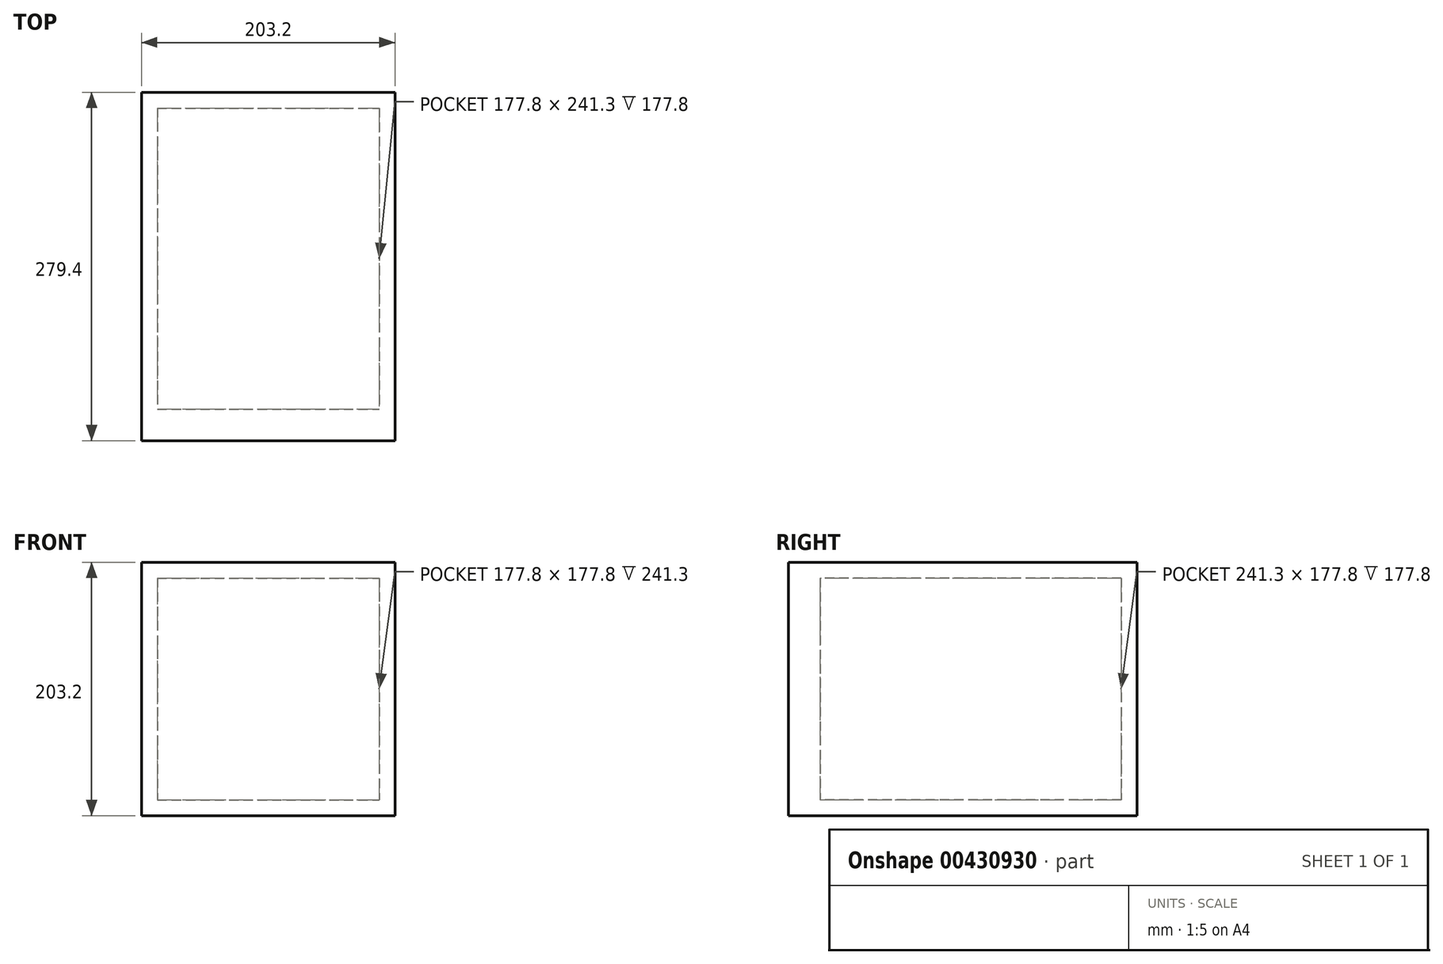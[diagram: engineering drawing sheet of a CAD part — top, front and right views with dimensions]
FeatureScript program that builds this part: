
annotation { "Feature Type Name" : "Feature", "Feature Type Description" : "" }
export const myFeature = defineFeature(function(context is Context, id is Id, definition is map)
    precondition{}
    {
        {
            var Q0;
            Q0=qCreatedBy(makeId("Top.planeOp"),FACE);
            var sketch = newSketch(context, id + "F0", { "sketchPlane" : qUnion([Q0])});
            skLineSegment(sketch, "E0.bottom", {"start": v(-126.86, 139.6) * mm, "end": v(76.34, 139.6) * mm});
            skLineSegment(sketch, "E0.top", {"start": v(-126.86, -114.4) * mm, "end": v(76.34, -114.4) * mm});
            skLineSegment(sketch, "E0.left", {"start": v(-126.86, 139.6) * mm, "end": v(-126.86, -114.4) * mm});
            skLineSegment(sketch, "E0.right", {"start": v(76.34, 139.6) * mm, "end": v(76.34, -114.4) * mm});
            skSolve(sketch);
        }
        {
            var Q0;
            Q0 = qSketchRegion(id + "F0", true);
            extrude(context, id + "F1", {"entities" : qUnion([Q0]), "depth" : 203.2 * mm});
        }
        {
            var Q0;
            Q0=makeQuery(id+"F1.opExtrude","SWEPT_FACE",FACE,{"disambiguationData":[OSD([sQuery(id+"F0.wireOp",EDGE,"E0.top")])]});
            shell(context, id + "F2", {"entities" : qUnion([Q0]), "thickness" : 12.7 * mm});
        }
        {
            var Q0;
            Q0=makeQuery(id+"F1.opExtrude","SWEPT_FACE",FACE,{"disambiguationData":[OSD([sQuery(id+"F0.wireOp",EDGE,"E0.top")])]});
            var sketch = newSketch(context, id + "F3", { "sketchPlane" : qUnion([Q0])});
            skLineSegment(sketch, "E1.bottom", {"start": v(-126.86, 203.2) * mm, "end": v(-25.26, 203.2) * mm});
            skLineSegment(sketch, "E1.top", {"start": v(-126.86, 0) * mm, "end": v(-25.26, 0) * mm});
            skLineSegment(sketch, "E1.left", {"start": v(-126.86, 203.2) * mm, "end": v(-126.86, 0) * mm});
            skLineSegment(sketch, "E1.right", {"start": v(-25.26, 203.2) * mm, "end": v(-25.26, 0) * mm});
            skLineSegment(sketch, "E2.bottom", {"start": v(-25.26, 203.2) * mm, "end": v(76.34, 203.2) * mm});
            skLineSegment(sketch, "E2.top", {"start": v(-25.26, 0) * mm, "end": v(76.34, 0) * mm});
            skLineSegment(sketch, "E2.right", {"start": v(76.34, 203.2) * mm, "end": v(76.34, 0) * mm});
            skSolve(sketch);
        }
        {
            var Q0;
            Q0 = qSketchRegion(id + "F3", true);
            extrude(context, id + "F4", {"entities" : qUnion([Q0]), "operationType" : NewBodyOperationType.ADD, "depth" : 25.4 * mm});
        }
    });
